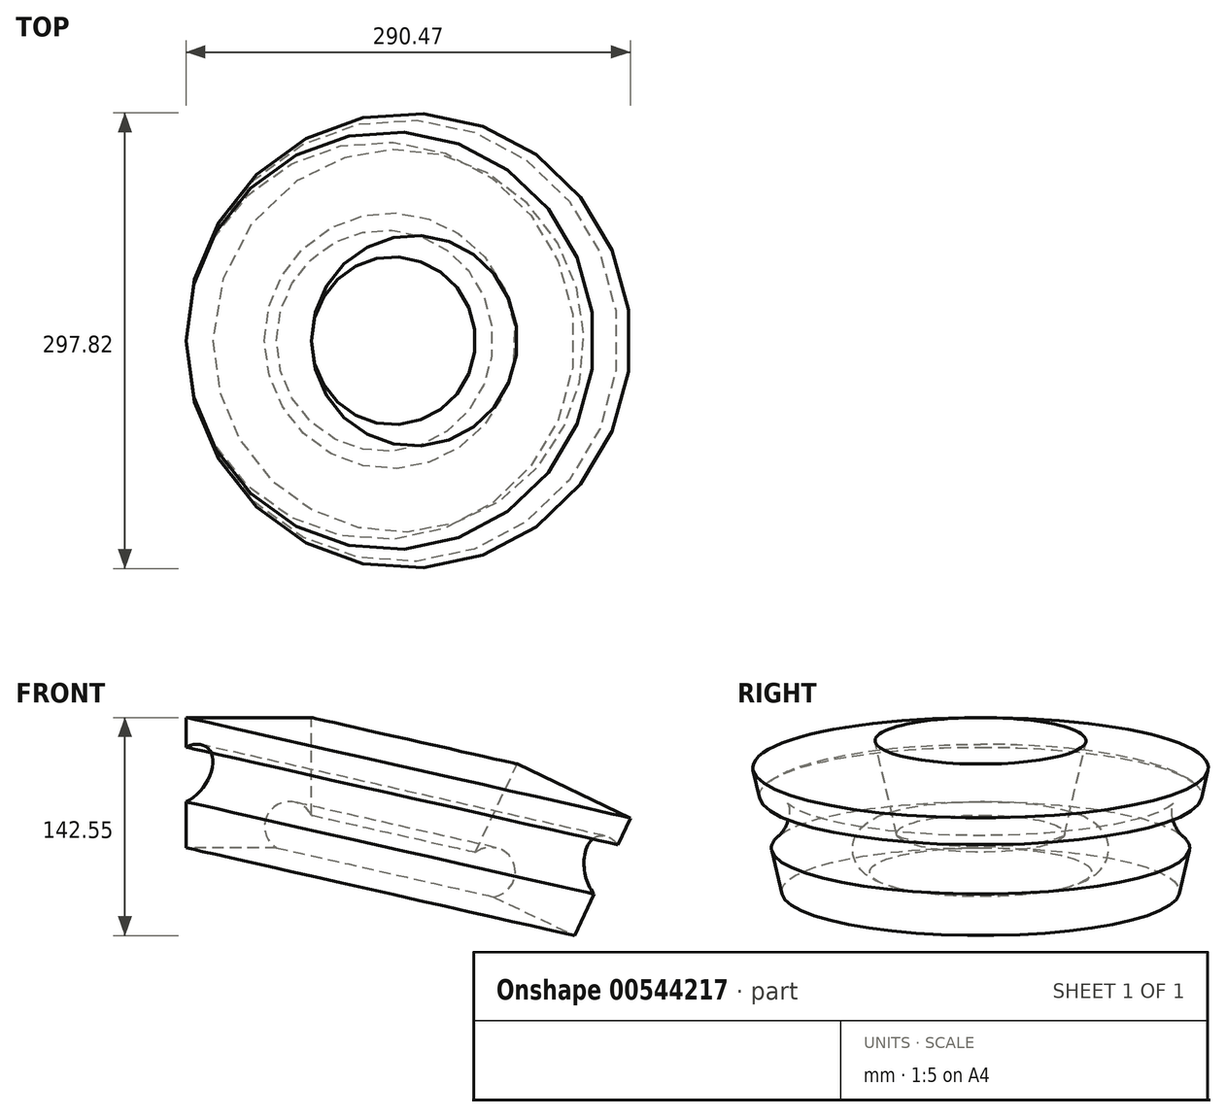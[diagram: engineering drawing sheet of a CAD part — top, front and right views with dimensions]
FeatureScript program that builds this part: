
annotation { "Feature Type Name" : "Feature", "Feature Type Description" : "" }
export const myFeature = defineFeature(function(context is Context, id is Id, definition is map)
    precondition{}
    {
        {
            var Q0;
            Q0=qCreatedBy(makeId("Front.planeOp"),FACE);
            var sketch = newSketch(context, id + "F0", { "sketchPlane" : qUnion([Q0])});
            skLineSegment(sketch, "E0", {"start": v(-37.1, 36.61) * mm, "end": v(-37.1, -48.53) * mm});
            skLineSegment(sketch, "E1", {"start": v(-37.1, -48.53) * mm, "end": v(44.82, -48.53) * mm});
            skLineSegment(sketch, "E2", {"start": v(44.82, -48.53) * mm, "end": v(44.82, 36.61) * mm});
            skLineSegment(sketch, "E3", {"start": v(44.82, 36.61) * mm, "end": v(-37.1, 36.61) * mm});
            skLineSegment(sketch, "E4", {"start": v(69.69, -166.2) * mm, "end": v(105.28, -8.86) * mm});
            skArc(sketch, "E5", {"start": v(44.82, -27.2) * mm, "mid": v(19.25, -22.71) * mm, "end": v(21.98, -48.53) * mm});
            skEllipse(sketch, "E6", {"center": v(-37.1, -0.6) * mm, "majorRadius": 22.36 * mm, "minorRadius": 13.99 * mm, "majorAxis": v(0.6, 0.8)});
            skSolve(sketch);
        }
        {
            var Q0;
            Q0=makeQuery(id+"F0.imprint","IMPRINT",FACE,{"disambiguationData":[TD([[makeQuery(id+"F0.imprint","IMPRINT",EDGE,{"derivedFrom":sQuery(id+"F0.wireOp",EDGE,"E0")}),1.0]])]});
            var Q1;
            Q1=sQuery(id+"F0.wireOp",EDGE,"E4");
            revolve(context, id + "F1", {"entities" : qUnion([Q0]), "axis" : qUnion([Q1]), "revolveType" : RevolveType.FULL});
        }
    });
